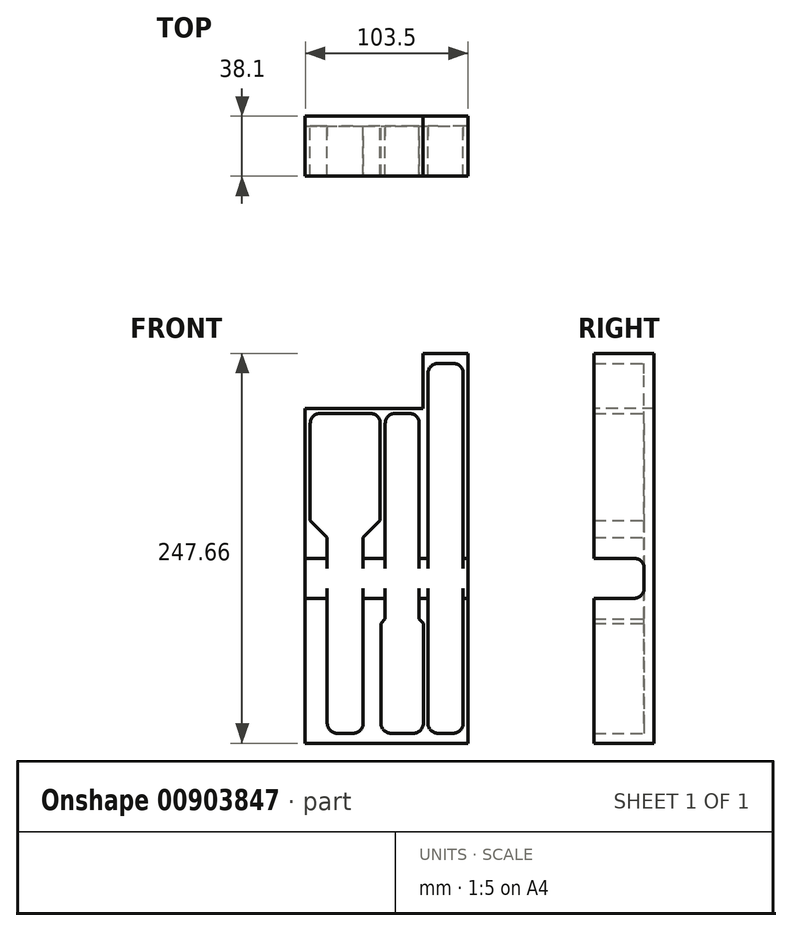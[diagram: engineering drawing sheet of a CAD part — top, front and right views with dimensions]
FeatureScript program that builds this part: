
annotation { "Feature Type Name" : "Feature", "Feature Type Description" : "" }
export const myFeature = defineFeature(function(context is Context, id is Id, definition is map)
    precondition{}
    {
        {
            var Q0;
            Q0=qCreatedBy(makeId("Front.planeOp"),FACE);
            var sketch = newSketch(context, id + "F0", { "sketchPlane" : qUnion([Q0])});
            skLineSegment(sketch, "E0.bottom", {"start": v(51.75, 123.83) * mm, "end": v(-51.75, 123.83) * mm});
            skLineSegment(sketch, "E0.top", {"start": v(51.75, -123.83) * mm, "end": v(-51.75, -123.83) * mm});
            skLineSegment(sketch, "E0.left", {"start": v(51.75, 123.83) * mm, "end": v(51.75, -123.83) * mm});
            skLineSegment(sketch, "E0.right", {"start": v(-51.75, 123.83) * mm, "end": v(-51.75, -123.83) * mm});
            skPoint(sketch, "E0.middle", {"position": v(0, 0) * mm});
            skSolve(sketch);
        }
        {
            var Q0;
            Q0 = qSketchRegion(id + "F0", true);
            extrude(context, id + "F1", {"entities" : qUnion([Q0]), "depth" : 31.75 * mm, "offsetDistance" : 25.4 * mm, "hasSecondDirection" : true, "secondDirectionOppositeDirection" : true, "secondDirectionDepth" : 6.35 * mm});
        }
        {
            var Q0;
            Q0=qCreatedBy(makeId("Front.planeOp"),FACE);
            var sketch = newSketch(context, id + "F2", { "sketchPlane" : qUnion([Q0])});
            skLineSegment(sketch, "E1.bottom", {"start": v(26.23, -117.48) * mm, "end": v(48.58, -117.48) * mm});
            skLineSegment(sketch, "E1.top", {"start": v(26.23, 117.47) * mm, "end": v(48.58, 117.47) * mm});
            skLineSegment(sketch, "E1.left", {"start": v(26.23, -117.48) * mm, "end": v(26.23, 117.47) * mm});
            skLineSegment(sketch, "E1.right", {"start": v(48.58, -117.48) * mm, "end": v(48.58, 117.47) * mm});
            skLineSegment(sketch, "E2", {"start": v(-0.95, 85.72) * mm, "end": v(20.64, 85.72) * mm});
            skLineSegment(sketch, "E3", {"start": v(20.64, 85.72) * mm, "end": v(20.64, -44.96) * mm});
            skLineSegment(sketch, "E4", {"start": v(20.64, -44.96) * mm, "end": v(23.3, -47.63) * mm});
            skLineSegment(sketch, "E5", {"start": v(23.3, -47.63) * mm, "end": v(23.3, -117.48) * mm});
            skLineSegment(sketch, "E6", {"start": v(23.3, -117.48) * mm, "end": v(-3.62, -117.48) * mm});
            skLineSegment(sketch, "E7", {"start": v(-3.62, -117.48) * mm, "end": v(-3.62, -47.63) * mm});
            skLineSegment(sketch, "E8", {"start": v(-3.62, -47.63) * mm, "end": v(-0.95, -44.96) * mm});
            skLineSegment(sketch, "E9", {"start": v(-0.95, -44.96) * mm, "end": v(-0.95, 85.72) * mm});
            skLineSegment(sketch, "E10", {"start": v(-37.78, -117.48) * mm, "end": v(-37.78, 6.86) * mm});
            skLineSegment(sketch, "E11", {"start": v(-37.78, 6.86) * mm, "end": v(-48.58, 17.65) * mm});
            skLineSegment(sketch, "E12", {"start": v(-48.58, 17.65) * mm, "end": v(-48.58, 85.72) * mm});
            skLineSegment(sketch, "E13", {"start": v(-48.58, 85.72) * mm, "end": v(-4.13, 85.72) * mm});
            skLineSegment(sketch, "E14", {"start": v(-4.13, 85.72) * mm, "end": v(-4.13, 17.65) * mm});
            skLineSegment(sketch, "E15", {"start": v(-4.13, 17.65) * mm, "end": v(-14.92, 6.86) * mm});
            skLineSegment(sketch, "E16", {"start": v(-14.92, 6.86) * mm, "end": v(-14.92, -117.48) * mm});
            skLineSegment(sketch, "E17", {"start": v(-14.92, -117.48) * mm, "end": v(-37.78, -117.48) * mm});
            skSolve(sketch);
        }
        {
            var Q0;
            Q0 = qSketchRegion(id + "F2", true);
            extrude(context, id + "F3", {"entities" : qUnion([Q0]), "operationType" : NewBodyOperationType.REMOVE, "endBound" : BoundingType.UP_TO_NEXT, "depth" : 25.4 * mm, "offsetDistance" : 25.4 * mm});
        }
        {
            var Q0;
            Q0=makeQuery(id+"F3.boolean.opBoolean","COPY",EDGE,{"derivedFrom":makeQuery(id+"F3.opExtrude","SWEPT_EDGE",EDGE,{"disambiguationData":[OSD([sQuery(id+"F2.wireOp",EDGE,"E12"),sQuery(id+"F2.wireOp",EDGE,"E13")])]})});
            var Q1;
            Q1=makeQuery(id+"F3.boolean.opBoolean","COPY",EDGE,{"derivedFrom":makeQuery(id+"F3.opExtrude","SWEPT_EDGE",EDGE,{"disambiguationData":[OSD([sQuery(id+"F2.wireOp",EDGE,"E13"),sQuery(id+"F2.wireOp",EDGE,"E14")])]})});
            var Q2;
            Q2=makeQuery(id+"F3.boolean.opBoolean","COPY",EDGE,{"derivedFrom":makeQuery(id+"F3.opExtrude","SWEPT_EDGE",EDGE,{"disambiguationData":[OSD([sQuery(id+"F2.wireOp",EDGE,"E2"),sQuery(id+"F2.wireOp",EDGE,"E3")])]})});
            var Q3;
            Q3=makeQuery(id+"F3.boolean.opBoolean","COPY",EDGE,{"derivedFrom":makeQuery(id+"F3.opExtrude","SWEPT_EDGE",EDGE,{"disambiguationData":[OSD([sQuery(id+"F2.wireOp",EDGE,"E2"),sQuery(id+"F2.wireOp",EDGE,"E9")])]})});
            var Q4;
            Q4=makeQuery(id+"F3.boolean.opBoolean","COPY",EDGE,{"derivedFrom":makeQuery(id+"F3.opExtrude","SWEPT_EDGE",EDGE,{"disambiguationData":[OSD([sQuery(id+"F2.wireOp",EDGE,"E16"),sQuery(id+"F2.wireOp",EDGE,"E17")])]})});
            var Q5;
            Q5=makeQuery(id+"F3.boolean.opBoolean","COPY",EDGE,{"derivedFrom":makeQuery(id+"F3.opExtrude","SWEPT_EDGE",EDGE,{"disambiguationData":[OSD([sQuery(id+"F2.wireOp",EDGE,"E10"),sQuery(id+"F2.wireOp",EDGE,"E17")])]})});
            var Q6;
            Q6=makeQuery(id+"F3.boolean.opBoolean","COPY",EDGE,{"derivedFrom":makeQuery(id+"F3.opExtrude","SWEPT_EDGE",EDGE,{"disambiguationData":[OSD([sQuery(id+"F2.wireOp",EDGE,"E5"),sQuery(id+"F2.wireOp",EDGE,"E6")])]})});
            var Q7;
            Q7=makeQuery(id+"F3.boolean.opBoolean","COPY",EDGE,{"derivedFrom":makeQuery(id+"F3.opExtrude","SWEPT_EDGE",EDGE,{"disambiguationData":[OSD([sQuery(id+"F2.wireOp",EDGE,"E6"),sQuery(id+"F2.wireOp",EDGE,"E7")])]})});
            var Q8;
            Q8=makeQuery(id+"F3.boolean.opBoolean","COPY",EDGE,{"derivedFrom":makeQuery(id+"F3.opExtrude","SWEPT_EDGE",EDGE,{"disambiguationData":[OSD([sQuery(id+"F2.wireOp",EDGE,"E1.top"),sQuery(id+"F2.wireOp",EDGE,"E1.right")])]})});
            var Q9;
            Q9=makeQuery(id+"F3.boolean.opBoolean","COPY",EDGE,{"derivedFrom":makeQuery(id+"F3.opExtrude","SWEPT_EDGE",EDGE,{"disambiguationData":[OSD([sQuery(id+"F2.wireOp",EDGE,"E1.top"),sQuery(id+"F2.wireOp",EDGE,"E1.left")])]})});
            var Q10;
            Q10=makeQuery(id+"F3.boolean.opBoolean","COPY",EDGE,{"derivedFrom":makeQuery(id+"F3.opExtrude","SWEPT_EDGE",EDGE,{"disambiguationData":[OSD([sQuery(id+"F2.wireOp",EDGE,"E1.bottom"),sQuery(id+"F2.wireOp",EDGE,"E1.left")])]})});
            var Q11;
            Q11=makeQuery(id+"F3.boolean.opBoolean","COPY",EDGE,{"derivedFrom":makeQuery(id+"F3.opExtrude","SWEPT_EDGE",EDGE,{"disambiguationData":[OSD([sQuery(id+"F2.wireOp",EDGE,"E1.bottom"),sQuery(id+"F2.wireOp",EDGE,"E1.right")])]})});
            fillet(context, id + "F4", {"entities" : qUnion([Q0, Q1, Q2, Q3, Q4, Q5, Q6, Q7, Q8, Q9, Q10, Q11]), "radius" : 6.35 * mm, "tangentPropagation" : true, "allowEdgeOverflow" : false});
        }
        {
            var Q0;
            Q0=makeQuery(id+"F1.opExtrude","CAP_FACE",FACE,{"disambiguationData":[OSD([sQuery(id+"F0.wireOp",EDGE,"E0.bottom"),sQuery(id+"F0.wireOp",EDGE,"E0.top"),sQuery(id+"F0.wireOp",EDGE,"E0.left"),sQuery(id+"F0.wireOp",EDGE,"E0.right")])],"isStart":false});
            var sketch = newSketch(context, id + "F5", { "sketchPlane" : qUnion([Q0])});
            skLineSegment(sketch, "E18", {"start": v(23.05, 123.83) * mm, "end": v(23.05, 88.9) * mm});
            skLineSegment(sketch, "E19", {"start": v(23.05, 88.9) * mm, "end": v(-51.75, 88.9) * mm});
            skLineSegment(sketch, "E20", {"start": v(-51.75, 88.9) * mm, "end": v(-51.75, 123.83) * mm});
            skLineSegment(sketch, "E21", {"start": v(-51.75, 123.83) * mm, "end": v(23.05, 123.83) * mm});
            skSolve(sketch);
        }
        {
            var Q0;
            Q0=makeQuery(id+"F5.imprint","IMPRINT",FACE,{"disambiguationData":[TD([[makeQuery(id+"F5.imprint","IMPRINT",EDGE,{"derivedFrom":sQuery(id+"F5.wireOp",EDGE,"E18")}),-1.0]])]});
            extrude(context, id + "F6", {"entities" : qUnion([Q0]), "operationType" : NewBodyOperationType.REMOVE, "endBound" : BoundingType.THROUGH_ALL, "oppositeDirection" : true, "depth" : 25.4 * mm, "offsetDistance" : 25.4 * mm});
        }
        {
            var Q0;
            Q0=makeQuery(id+"F1.opExtrude","CAP_FACE",FACE,{"disambiguationData":[OSD([sQuery(id+"F0.wireOp",EDGE,"E0.bottom"),sQuery(id+"F0.wireOp",EDGE,"E0.top"),sQuery(id+"F0.wireOp",EDGE,"E0.left"),sQuery(id+"F0.wireOp",EDGE,"E0.right")])],"isStart":false});
            var sketch = newSketch(context, id + "F7", { "sketchPlane" : qUnion([Q0])});
            skLineSegment(sketch, "E22", {"start": v(51.75, -31.75) * mm, "end": v(-51.75, -31.75) * mm});
            skLineSegment(sketch, "E23", {"start": v(-51.75, -31.75) * mm, "end": v(-51.75, -6.35) * mm});
            skLineSegment(sketch, "E24", {"start": v(-51.75, -6.35) * mm, "end": v(51.75, -6.35) * mm});
            skLineSegment(sketch, "E25", {"start": v(51.75, -31.75) * mm, "end": v(51.75, -6.35) * mm});
            skLineSegment(sketch, "E26", {"start": v(-14.92, -6.35) * mm, "end": v(-14.92, 6.86) * mm, "construction": true});
            skLineSegment(sketch, "E27", {"start": v(-0.95, -31.75) * mm, "end": v(-0.95, -44.96) * mm, "construction": true});
            skSolve(sketch);
        }
        {
            var Q0;
            Q0 = qSketchRegion(id + "F7", true);
            extrude(context, id + "F8", {"entities" : qUnion([Q0]), "operationType" : NewBodyOperationType.REMOVE, "oppositeDirection" : true, "depth" : 31.75 * mm, "offsetDistance" : 25.4 * mm});
        }
        {
            var Q0;
            {var subQ1=sQuery(id+"F7.wireOp",EDGE,"E24");Q0=makeQuery(id+"F8.boolean.opBoolean","COPY",EDGE,{"disambiguationData":[TD([makeQuery(id+"F1.opExtrude","SWEPT_FACE",FACE,{"disambiguationData":[OSD([sQuery(id+"F0.wireOp",EDGE,"E0.right")])]})])],"derivedFrom":makeQuery(id+"F8.opExtrude","CAP_EDGE",EDGE,{"disambiguationData":[OSD([subQ1])],"isStart":false})});}
            var Q1;
            {var subQ1=sQuery(id+"F7.wireOp",EDGE,"E22");Q1=makeQuery(id+"F8.boolean.opBoolean","COPY",EDGE,{"disambiguationData":[TD([makeQuery(id+"F1.opExtrude","SWEPT_FACE",FACE,{"disambiguationData":[OSD([sQuery(id+"F0.wireOp",EDGE,"E0.right")])]})])],"derivedFrom":makeQuery(id+"F8.opExtrude","CAP_EDGE",EDGE,{"disambiguationData":[OSD([subQ1])],"isStart":false})});}
            var Q2;
            {var subQ1=sQuery(id+"F2.wireOp",EDGE,"E9");var subQ2=sQuery(id+"F7.wireOp",EDGE,"E24");Q2=makeQuery(id+"F8.boolean.opBoolean","COPY",EDGE,{"disambiguationData":[TD([makeQuery(id+"F3.boolean.opBoolean","COPY",FACE,{"derivedFrom":makeQuery(id+"F3.opExtrude","SWEPT_FACE",FACE,{"disambiguationData":[OSD([subQ1])]})})])],"derivedFrom":makeQuery(id+"F8.opExtrude","CAP_EDGE",EDGE,{"disambiguationData":[OSD([subQ2])],"isStart":false})});}
            var Q3;
            {var subQ1=sQuery(id+"F2.wireOp",EDGE,"E9");var subQ2=sQuery(id+"F7.wireOp",EDGE,"E22");Q3=makeQuery(id+"F8.boolean.opBoolean","COPY",EDGE,{"disambiguationData":[TD([makeQuery(id+"F3.boolean.opBoolean","COPY",FACE,{"derivedFrom":makeQuery(id+"F3.opExtrude","SWEPT_FACE",FACE,{"disambiguationData":[OSD([subQ1])]})})])],"derivedFrom":makeQuery(id+"F8.opExtrude","CAP_EDGE",EDGE,{"disambiguationData":[OSD([subQ2])],"isStart":false})});}
            var Q4;
            {var subQ1=sQuery(id+"F2.wireOp",EDGE,"E1.left");var subQ2=sQuery(id+"F7.wireOp",EDGE,"E24");Q4=makeQuery(id+"F8.boolean.opBoolean","COPY",EDGE,{"disambiguationData":[TD([makeQuery(id+"F3.boolean.opBoolean","COPY",FACE,{"derivedFrom":makeQuery(id+"F3.opExtrude","SWEPT_FACE",FACE,{"disambiguationData":[OSD([subQ1])]})})])],"derivedFrom":makeQuery(id+"F8.opExtrude","CAP_EDGE",EDGE,{"disambiguationData":[OSD([subQ2])],"isStart":false})});}
            var Q5;
            {var subQ1=sQuery(id+"F2.wireOp",EDGE,"E1.left");var subQ2=sQuery(id+"F7.wireOp",EDGE,"E22");Q5=makeQuery(id+"F8.boolean.opBoolean","COPY",EDGE,{"disambiguationData":[TD([makeQuery(id+"F3.boolean.opBoolean","COPY",FACE,{"derivedFrom":makeQuery(id+"F3.opExtrude","SWEPT_FACE",FACE,{"disambiguationData":[OSD([subQ1])]})})])],"derivedFrom":makeQuery(id+"F8.opExtrude","CAP_EDGE",EDGE,{"disambiguationData":[OSD([subQ2])],"isStart":false})});}
            var Q6;
            {var subQ1=sQuery(id+"F7.wireOp",EDGE,"E24");Q6=makeQuery(id+"F8.boolean.opBoolean","COPY",EDGE,{"disambiguationData":[TD([makeQuery(id+"F1.opExtrude","SWEPT_FACE",FACE,{"disambiguationData":[OSD([sQuery(id+"F0.wireOp",EDGE,"E0.left")])]})])],"derivedFrom":makeQuery(id+"F8.opExtrude","CAP_EDGE",EDGE,{"disambiguationData":[OSD([subQ1])],"isStart":false})});}
            var Q7;
            {var subQ1=sQuery(id+"F7.wireOp",EDGE,"E22");Q7=makeQuery(id+"F8.boolean.opBoolean","COPY",EDGE,{"disambiguationData":[TD([makeQuery(id+"F1.opExtrude","SWEPT_FACE",FACE,{"disambiguationData":[OSD([sQuery(id+"F0.wireOp",EDGE,"E0.left")])]})])],"derivedFrom":makeQuery(id+"F8.opExtrude","CAP_EDGE",EDGE,{"disambiguationData":[OSD([subQ1])],"isStart":false})});}
            fillet(context, id + "F9", {"entities" : qUnion([Q0, Q1, Q2, Q3, Q4, Q5, Q6, Q7]), "radius" : 6.35 * mm, "tangentPropagation" : true, "allowEdgeOverflow" : false});
        }
    });
